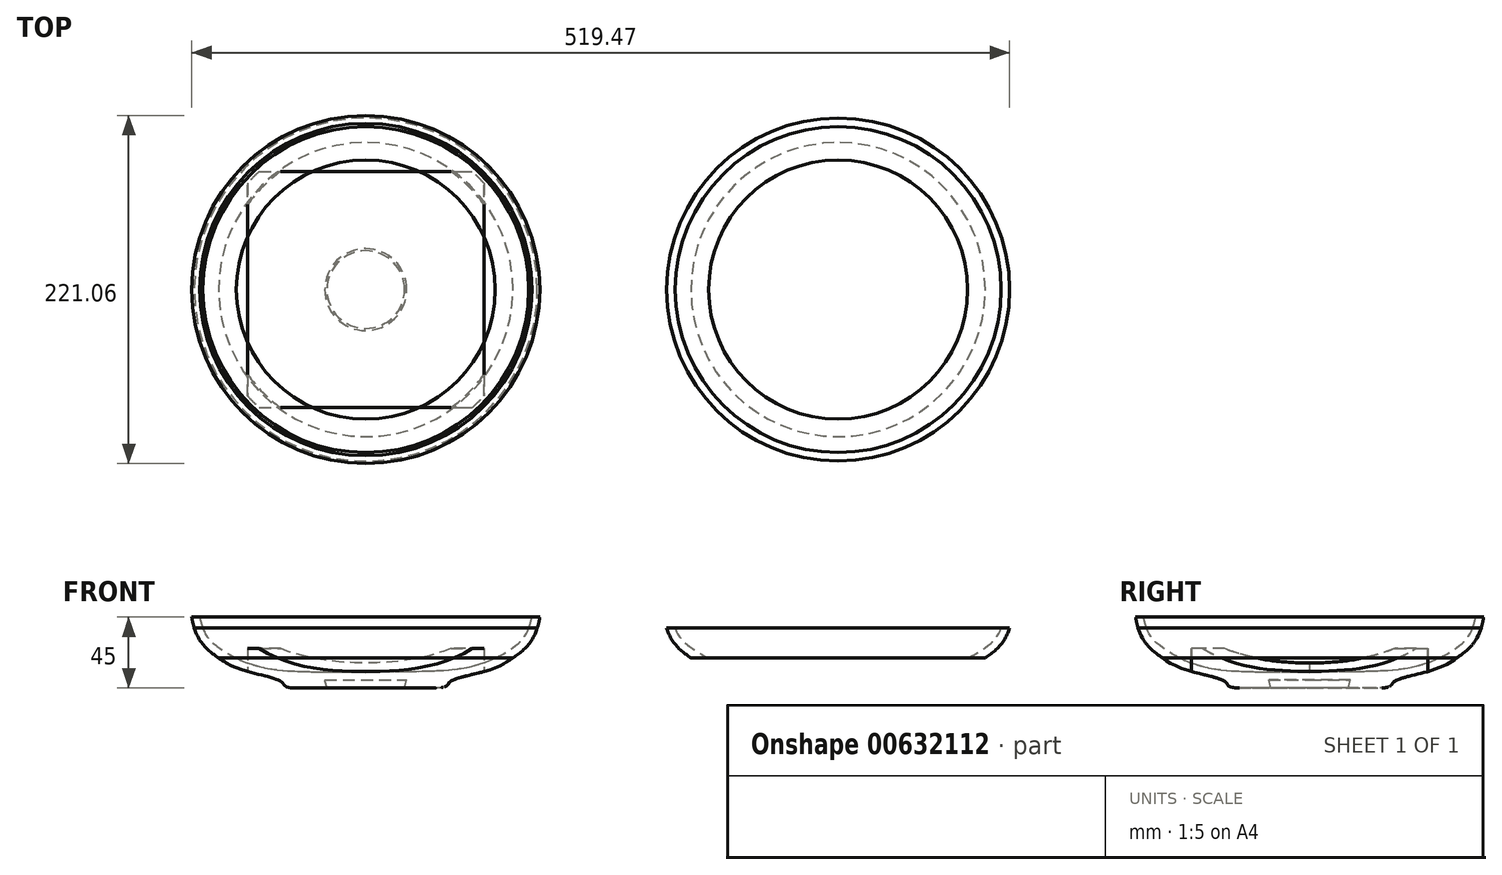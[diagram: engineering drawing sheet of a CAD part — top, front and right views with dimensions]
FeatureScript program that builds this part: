
annotation { "Feature Type Name" : "Feature", "Feature Type Description" : "" }
export const myFeature = defineFeature(function(context is Context, id is Id, definition is map)
    precondition{}
    {
        {
            var Q0;
            Q0=qCreatedBy(makeId("Front.planeOp"),FACE);
            var sketch = newSketch(context, id + "F0", { "sketchPlane" : qUnion([Q0])});
            skLineSegment(sketch, "E0", {"start": v(0, -21.13) * mm, "end": v(0, 72.26) * mm, "construction": true});
            skLineSegment(sketch, "E1.bottom", {"start": v(0, 0) * mm, "end": v(112.5, 0) * mm, "construction": true});
            skLineSegment(sketch, "E1.top", {"start": v(0, 75) * mm, "end": v(112.5, 75) * mm, "construction": true});
            skLineSegment(sketch, "E1.left", {"start": v(0, 0) * mm, "end": v(0, 75) * mm, "construction": true});
            skLineSegment(sketch, "E1.right", {"start": v(112.5, 0) * mm, "end": v(112.5, 75) * mm, "construction": true});
            skLineSegment(sketch, "E2", {"start": v(0, 5) * mm, "end": v(26, 5) * mm});
            skLineSegment(sketch, "E3", {"start": v(26, 5) * mm, "end": v(24.66, 0) * mm});
            skLineSegment(sketch, "E4", {"start": v(24.66, 0) * mm, "end": v(44.66, 0) * mm});
            skFitSpline(sketch, "E5", {"points": [v(44.66, 0) * mm, v(53.49, 3.84) * mm, v(78.12, 11.34) * mm, v(95.39, 20.4) * mm, v(110.53, 45) * mm], "startDerivative": vector(138.62, 0) * mm, "endDerivative": vector(21.54, 144.6) * mm});
            skLineSegment(sketch, "E6", {"start": v(110.53, 45) * mm, "end": v(105.53, 45) * mm});
            skFitSpline(sketch, "E7", {"points": [v(105.53, 45) * mm, v(96.05, 27.68) * mm, v(72.17, 14.88) * mm, v(35.66, 10.35) * mm, v(0, 10) * mm], "startDerivative": vector(-36.44, -154.34) * mm, "endDerivative": vector(-118.09, -1.6) * mm});
            skLineSegment(sketch, "E8", {"start": v(0, 10) * mm, "end": v(0, 5) * mm});
            skSolve(sketch);
        }
        {
            var Q0;
            Q0=qCreatedBy(makeId("Front.planeOp"),FACE);
            var sketch = newSketch(context, id + "F1", { "sketchPlane" : qUnion([Q0])});
            skLineSegment(sketch, "E9.bottom", {"start": v(0, 0) * mm, "end": v(75, 0) * mm});
            skLineSegment(sketch, "E9.top", {"start": v(0, 25) * mm, "end": v(75, 25) * mm});
            skLineSegment(sketch, "E9.left", {"start": v(0, 0) * mm, "end": v(0, 25) * mm});
            skLineSegment(sketch, "E9.right", {"start": v(75, 0) * mm, "end": v(75, 25) * mm});
            skLineSegment(sketch, "E10.bottom", {"start": v(0, 0) * mm, "end": v(-75, 0) * mm});
            skLineSegment(sketch, "E10.top", {"start": v(0, 25) * mm, "end": v(-75, 25) * mm});
            skLineSegment(sketch, "E10.right", {"start": v(-75, 0) * mm, "end": v(-75, 25) * mm});
            skSolve(sketch);
        }
        {
            var Q0;
            Q0 = qSketchRegion(id + "F1", true);
            extrude(context, id + "F2", {"entities" : qUnion([Q0]), "endBound" : BoundingType.SYMMETRIC, "oppositeDirection" : true, "depth" : 150 * mm, "offsetDistance" : 25 * mm});
        }
        {
            var Q0;
            Q0 = qSketchRegion(id + "F1", true);
            extrude(context, id + "F3", {"entities" : qUnion([Q0]), "operationType" : NewBodyOperationType.ADD, "depth" : 25 * mm, "offsetDistance" : 25 * mm});
        }
        {
            var Q0;
            Q0=qCreatedBy(makeId("Top.planeOp"),FACE);
            var sketch = newSketch(context, id + "F4", { "sketchPlane" : qUnion([Q0])});
            skCircle(sketch, "E11", {"center": v(709.54, 0) * mm, "radius": 125 * mm});
            skCircle(sketch, "E12.0", {"center": v(709.54, 0) * mm, "radius": 110 * mm});
            skCircle(sketch, "E13.0", {"center": v(709.54, 0) * mm, "radius": 95 * mm});
            skCircle(sketch, "E14.0", {"center": v(709.54, 0) * mm, "radius": 80 * mm});
            skCircle(sketch, "E15.0", {"center": v(709.54, 0) * mm, "radius": 65 * mm});
            skCircle(sketch, "E16.0", {"center": v(709.54, 0) * mm, "radius": 50 * mm});
            skCircle(sketch, "E17.0", {"center": v(709.54, 0) * mm, "radius": 35 * mm});
            skCircle(sketch, "E18", {"center": v(1132.22, -0.6) * mm, "radius": 125 * mm});
            skCircle(sketch, "E19.0", {"center": v(1132.22, -0.6) * mm, "radius": 110 * mm});
            skCircle(sketch, "E20.0", {"center": v(1132.22, -0.6) * mm, "radius": 95 * mm});
            skCircle(sketch, "E21.0", {"center": v(1132.22, -0.6) * mm, "radius": 80 * mm});
            skCircle(sketch, "E22.0", {"center": v(1132.22, -0.6) * mm, "radius": 65 * mm});
            skCircle(sketch, "E23.0", {"center": v(1132.22, -0.6) * mm, "radius": 50 * mm});
            skCircle(sketch, "E24.0", {"center": v(1132.22, -0.6) * mm, "radius": 35 * mm});
            skSolve(sketch);
        }
        {
            var Q0;
            Q0=makeQuery(id+"F4.imprint","IMPRINT",FACE,{"disambiguationData":[TD([[makeQuery(id+"F4.imprint","IMPRINT",EDGE,{"derivedFrom":sQuery(id+"F4.wireOp",EDGE,"E11")}),1.0]])]});
            var Q1;
            Q1=makeQuery(id+"F4.imprint","IMPRINT",FACE,{"disambiguationData":[TD([[makeQuery(id+"F4.imprint","IMPRINT",EDGE,{"derivedFrom":sQuery(id+"F4.wireOp",EDGE,"E12.0")}),1.0]])]});
            extrude(context, id + "F5", {"entities" : qUnion([Q0, Q1]), "depth" : 19 * mm, "offsetDistance" : 25 * mm});
        }
        {
            var Q0;
            Q0=makeQuery(id+"F4.imprint","IMPRINT",FACE,{"disambiguationData":[TD([[makeQuery(id+"F4.imprint","IMPRINT",EDGE,{"derivedFrom":sQuery(id+"F4.wireOp",EDGE,"E12.0")}),1.0]])]});
            var Q1;
            Q1=makeQuery(id+"F4.imprint","IMPRINT",FACE,{"disambiguationData":[TD([[makeQuery(id+"F4.imprint","IMPRINT",EDGE,{"derivedFrom":sQuery(id+"F4.wireOp",EDGE,"E13.0")}),1.0]])]});
            extrude(context, id + "F6", {"entities" : qUnion([Q0, Q1]), "depth" : 19 * mm, "offsetDistance" : 25 * mm});
        }
        {
            var Q0;
            Q0=makeQuery(id+"F4.imprint","IMPRINT",FACE,{"disambiguationData":[TD([[makeQuery(id+"F4.imprint","IMPRINT",EDGE,{"derivedFrom":sQuery(id+"F4.wireOp",EDGE,"E13.0")}),1.0]])]});
            var Q1;
            Q1=makeQuery(id+"F4.imprint","IMPRINT",FACE,{"disambiguationData":[TD([[makeQuery(id+"F4.imprint","IMPRINT",EDGE,{"derivedFrom":sQuery(id+"F4.wireOp",EDGE,"E14.0")}),1.0]])]});
            extrude(context, id + "F7", {"entities" : qUnion([Q0, Q1]), "depth" : 19 * mm, "offsetDistance" : 25 * mm});
        }
        {
            var Q0;
            Q0=makeQuery(id+"F4.imprint","IMPRINT",FACE,{"disambiguationData":[TD([[makeQuery(id+"F4.imprint","IMPRINT",EDGE,{"derivedFrom":sQuery(id+"F4.wireOp",EDGE,"E14.0")}),1.0]])]});
            var Q1;
            Q1=makeQuery(id+"F4.imprint","IMPRINT",FACE,{"disambiguationData":[TD([[makeQuery(id+"F4.imprint","IMPRINT",EDGE,{"derivedFrom":sQuery(id+"F4.wireOp",EDGE,"E15.0")}),1.0]])]});
            extrude(context, id + "F8", {"entities" : qUnion([Q0, Q1]), "depth" : 19 * mm, "offsetDistance" : 25 * mm});
        }
        {
            var Q0;
            Q0=makeQuery(id+"F4.imprint","IMPRINT",FACE,{"disambiguationData":[TD([[makeQuery(id+"F4.imprint","IMPRINT",EDGE,{"derivedFrom":sQuery(id+"F4.wireOp",EDGE,"E16.0")}),1.0]])]});
            var Q1;
            Q1=makeQuery(id+"F4.imprint","IMPRINT",FACE,{"disambiguationData":[TD([[makeQuery(id+"F4.imprint","IMPRINT",EDGE,{"derivedFrom":sQuery(id+"F4.wireOp",EDGE,"E15.0")}),1.0]])]});
            extrude(context, id + "F9", {"entities" : qUnion([Q0, Q1]), "depth" : 19 * mm, "offsetDistance" : 25 * mm});
        }
        {
            var Q0;
            Q0=makeQuery(id+"F4.imprint","IMPRINT",FACE,{"disambiguationData":[TD([[makeQuery(id+"F4.imprint","IMPRINT",EDGE,{"derivedFrom":sQuery(id+"F4.wireOp",EDGE,"E16.0")}),1.0]])]});
            var Q1;
            Q1=makeQuery(id+"F4.imprint","IMPRINT",FACE,{"disambiguationData":[TD([[makeQuery(id+"F4.imprint","IMPRINT",EDGE,{"derivedFrom":sQuery(id+"F4.wireOp",EDGE,"E17.0")}),1.0]])]});
            extrude(context, id + "F10", {"entities" : qUnion([Q0, Q1]), "depth" : 19 * mm, "offsetDistance" : 25 * mm});
        }
        {
            var Q0;
            Q0=makeQuery(id+"F9.opExtrude","SWEPT_BODY",BODY,{"disambiguationData":[OSD([sQuery(id+"F4.wireOp",EDGE,"E15.0"),sQuery(id+"F4.wireOp",EDGE,"E17.0")])]});
            var Q1;
            Q1=sQuery(id+"F0.wireOp",EDGE,"E1.right");
            transform(context, id + "F11", {"entities" : qUnion([Q0]), "transformType" : TransformType.TRANSLATION_DISTANCE, "transformDirection" : qUnion([Q1]), "distance" : 19 * mm, "makeCopy" : false});
        }
        {
            var Q0;
            Q0=makeQuery(id+"F8.opExtrude","SWEPT_BODY",BODY,{"disambiguationData":[OSD([sQuery(id+"F4.wireOp",EDGE,"E14.0"),sQuery(id+"F4.wireOp",EDGE,"E16.0")])]});
            var Q1;
            Q1=sQuery(id+"F0.wireOp",EDGE,"E1.right");
            transform(context, id + "F12", {"entities" : qUnion([Q0]), "transformType" : TransformType.TRANSLATION_DISTANCE, "transformDirection" : qUnion([Q1]), "distance" : 38 * mm, "makeCopy" : false});
        }
        {
            var Q0;
            Q0=makeQuery(id+"F7.opExtrude","SWEPT_BODY",BODY,{"disambiguationData":[OSD([sQuery(id+"F4.wireOp",EDGE,"E13.0"),sQuery(id+"F4.wireOp",EDGE,"E15.0")])]});
            var Q1;
            Q1=sQuery(id+"F0.wireOp",EDGE,"E1.right");
            transform(context, id + "F13", {"entities" : qUnion([Q0]), "transformType" : TransformType.TRANSLATION_DISTANCE, "transformDirection" : qUnion([Q1]), "distance" : 57 * mm, "makeCopy" : false});
        }
        {
            var Q0;
            Q0=makeQuery(id+"F6.opExtrude","SWEPT_BODY",BODY,{"disambiguationData":[OSD([sQuery(id+"F4.wireOp",EDGE,"E12.0"),sQuery(id+"F4.wireOp",EDGE,"E14.0")])]});
            var Q1;
            Q1=sQuery(id+"F0.wireOp",EDGE,"E1.right");
            transform(context, id + "F14", {"entities" : qUnion([Q0]), "transformType" : TransformType.TRANSLATION_DISTANCE, "transformDirection" : qUnion([Q1]), "distance" : 76 * mm, "makeCopy" : false});
        }
        {
            var Q0;
            Q0=makeQuery(id+"F5.opExtrude","SWEPT_BODY",BODY,{"disambiguationData":[OSD([sQuery(id+"F4.wireOp",EDGE,"E11"),sQuery(id+"F4.wireOp",EDGE,"E13.0")])]});
            var Q1;
            Q1=sQuery(id+"F0.wireOp",EDGE,"E1.right");
            transform(context, id + "F15", {"entities" : qUnion([Q0]), "transformType" : TransformType.TRANSLATION_DISTANCE, "transformDirection" : qUnion([Q1]), "distance" : 95 * mm, "makeCopy" : false});
        }
        {
            var Q0;
            Q0=qCreatedBy(makeId("Front.planeOp"),FACE);
            var sketch = newSketch(context, id + "F16", { "sketchPlane" : qUnion([Q0])});
            skLineSegment(sketch, "E25.bottom", {"start": v(0, 0) * mm, "end": v(100, 0) * mm});
            skLineSegment(sketch, "E25.top", {"start": v(0, 19) * mm, "end": v(100, 19) * mm});
            skLineSegment(sketch, "E25.left", {"start": v(0, 0) * mm, "end": v(0, 19) * mm});
            skLineSegment(sketch, "E25.right", {"start": v(100, 0) * mm, "end": v(100, 19) * mm});
            skLineSegment(sketch, "E26.bottom", {"start": v(76.22, 19) * mm, "end": v(111.22, 19) * mm});
            skLineSegment(sketch, "E26.top", {"start": v(76.22, 38) * mm, "end": v(111.22, 38) * mm});
            skLineSegment(sketch, "E26.left", {"start": v(76.22, 19) * mm, "end": v(76.22, 38) * mm});
            skLineSegment(sketch, "E26.right", {"start": v(111.22, 19) * mm, "end": v(111.22, 38) * mm});
            skLineSegment(sketch, "E27.bottom", {"start": v(98.24, 38) * mm, "end": v(118.24, 38) * mm});
            skLineSegment(sketch, "E27.top", {"start": v(98.24, 57) * mm, "end": v(118.24, 57) * mm});
            skLineSegment(sketch, "E27.left", {"start": v(98.24, 38) * mm, "end": v(98.24, 57) * mm});
            skLineSegment(sketch, "E27.right", {"start": v(118.24, 38) * mm, "end": v(118.24, 57) * mm});
            skSolve(sketch);
        }
        {
            var Q0;
            Q0=makeQuery(id+"F16.imprint","IMPRINT",FACE,{"disambiguationData":[TD([[makeQuery(id+"F16.imprint","IMPRINT",EDGE,{"derivedFrom":sQuery(id+"F16.wireOp",EDGE,"E25.bottom")}),1.0]])]});
            var Q1;
            Q1=sQuery(id+"F0.wireOp",EDGE,"E1.left");
            revolve(context, id + "F17", {"entities" : qUnion([Q0]), "axis" : qUnion([Q1]), "revolveType" : RevolveType.FULL});
        }
        {
            var Q0;
            {var subQ1=sQuery(id+"F16.wireOp",EDGE,"E26.top");Q0=makeQuery(id+"F16.imprint","IMPRINT",FACE,{"disambiguationData":[TD([[makeQuery(id+"F16.imprint","IMPRINT",EDGE,{"derivedFrom":subQ1}),-1.0]])]});}
            var Q1;
            Q1=sQuery(id+"F0.wireOp",EDGE,"E1.left");
            revolve(context, id + "F18", {"entities" : qUnion([Q0]), "axis" : qUnion([Q1]), "revolveType" : RevolveType.FULL});
        }
        {
            var Q0;
            Q0=makeQuery(id+"F16.imprint","IMPRINT",FACE,{"disambiguationData":[TD([[makeQuery(id+"F16.imprint","IMPRINT",EDGE,{"derivedFrom":sQuery(id+"F16.wireOp",EDGE,"E27.top")}),-1.0]])]});
            var Q1;
            Q1=sQuery(id+"F0.wireOp",EDGE,"E1.left");
            revolve(context, id + "F19", {"entities" : qUnion([Q0]), "axis" : qUnion([Q1]), "revolveType" : RevolveType.FULL});
        }
        {
            var Q0;
            Q0 = qSketchRegion(id + "F0", true);
            var Q1;
            Q1=sQuery(id+"F0.wireOp",EDGE,"E1.left");
            revolve(context, id + "F20", {"operationType" : NewBodyOperationType.INTERSECT, "entities" : qUnion([Q0]), "axis" : qUnion([Q1]), "revolveType" : RevolveType.FULL});
        }
        {
            var Q0;
            Q0=makeQuery(id+"F18.opRevolve","SWEPT_BODY",BODY,{"disambiguationData":[OSD([sQuery(id+"F16.wireOp",EDGE,"E26.bottom"),sQuery(id+"F16.wireOp",EDGE,"E26.top"),sQuery(id+"F16.wireOp",EDGE,"E26.left"),sQuery(id+"F16.wireOp",EDGE,"E26.right"),sQuery(id+"F16.wireOp",EDGE,"E27.bottom")])]});
            var Q1;
            Q1=sQuery(id+"F0.wireOp",EDGE,"E1.bottom");
            transform(context, id + "F21", {"entities" : qUnion([Q0]), "transformType" : TransformType.TRANSLATION_DISTANCE, "transformDirection" : qUnion([Q1]), "distance" : 300 * mm, "makeCopy" : true});
        }
    });
